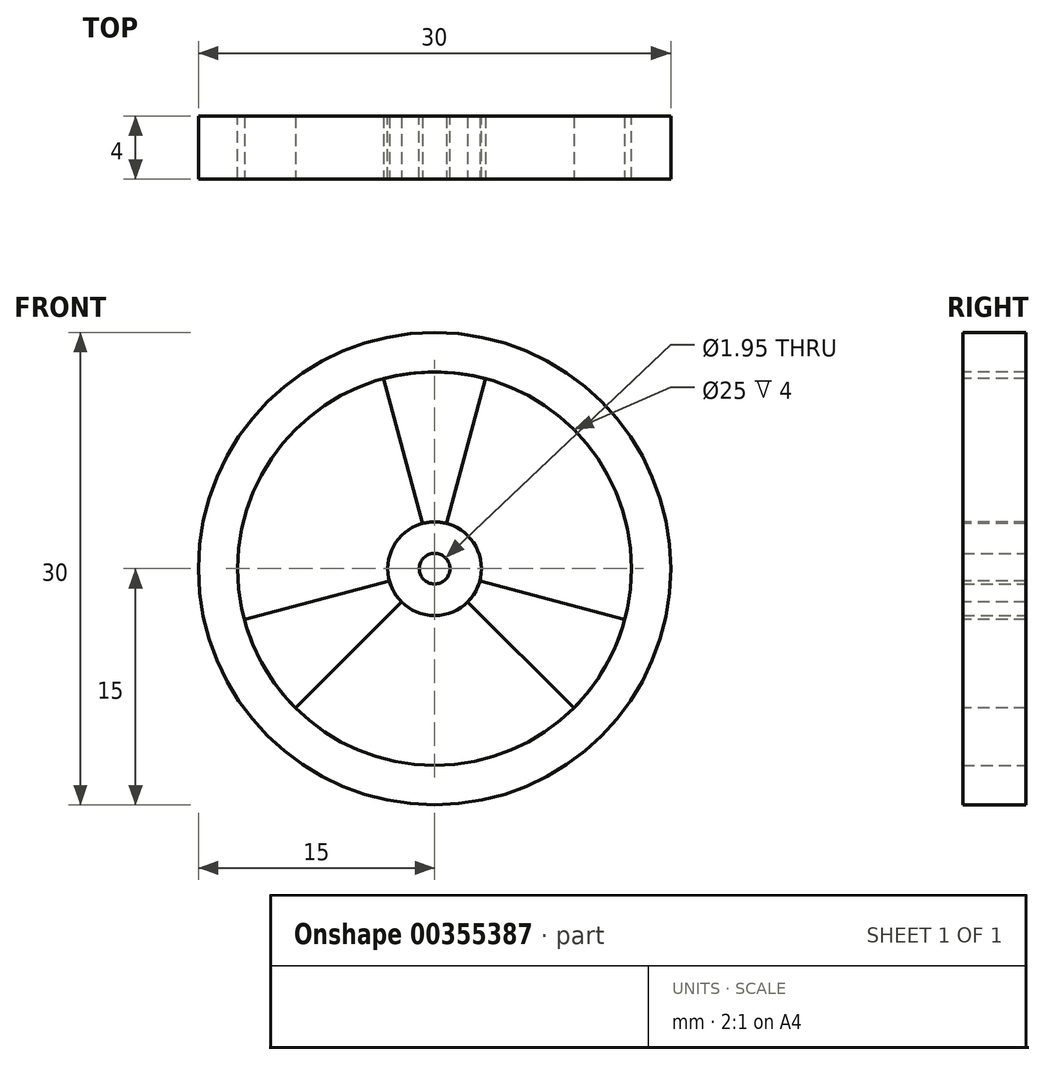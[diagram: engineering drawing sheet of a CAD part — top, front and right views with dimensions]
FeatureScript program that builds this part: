
annotation { "Feature Type Name" : "Feature", "Feature Type Description" : "" }
export const myFeature = defineFeature(function(context is Context, id is Id, definition is map)
    precondition{}
    {
        {
            var Q0;
            Q0=qCreatedBy(makeId("Front.planeOp"),FACE);
            var sketch = newSketch(context, id + "F0", { "sketchPlane" : qUnion([Q0])});
            skCircle(sketch, "E0", {"center": v(0, 0) * mm, "radius": 15 * mm});
            skCircle(sketch, "E1", {"center": v(0, 0) * mm, "radius": 0.97 * mm});
            skCircle(sketch, "E2", {"center": v(0, 0) * mm, "radius": 2.98 * mm});
            skCircle(sketch, "E3", {"center": v(0, 0) * mm, "radius": 12.5 * mm});
            skSolve(sketch);
        }
        {
            var Q0;
            Q0=qSketchRegion(id+"F0",true);
            var Q1;
            Q1=makeQuery(id+"F0.imprint","IMPRINT",FACE,{"disambiguationData":[TD([[makeQuery(id+"F0.imprint","IMPRINT",EDGE,{"derivedFrom":sQuery(id+"F0.wireOp",EDGE,"E1")}),-1.0]])]});
            extrude(context, id + "F1", {"entities" : qUnion([Q0, Q1]), "depth" : 4 * mm});
        }
        {
            var Q0;
            Q0=makeQuery(id+"F1.opExtrude","CAP_FACE",FACE,{"disambiguationData":[OSD([sQuery(id+"F0.wireOp",EDGE,"E0"),sQuery(id+"F0.wireOp",EDGE,"E1")])],"isStart":false});
            var sketch = newSketch(context, id + "F2", { "sketchPlane" : qUnion([Q0])});
            skArc(sketch, "E4", {"start": v(0.77, 2.87) * mm, "mid": v(0, 2.98) * mm, "end": v(-0.77, 2.87) * mm});
            skArc(sketch, "E5", {"start": v(3.24, 12.07) * mm, "mid": v(0, 12.5) * mm, "end": v(-3.24, 12.07) * mm});
            skLineSegment(sketch, "E6", {"start": v(0.77, 2.87) * mm, "end": v(3.24, 12.07) * mm});
            skLineSegment(sketch, "E7", {"start": v(3.24, 12.07) * mm, "end": v(0.77, 2.87) * mm});
            skLineSegment(sketch, "E8", {"start": v(-0.77, 2.87) * mm, "end": v(-3.24, 12.07) * mm});
            skSolve(sketch);
        }
        {
            var Q0;
            Q0=qSketchRegion(id+"F2",true);
            extrude(context, id + "F3", {"entities" : qUnion([Q0]), "oppositeDirection" : true, "depth" : 4 * mm});
        }
        {
            var Q0;
            Q0=makeQuery(id+"F3.opExtrude","SWEPT_BODY",BODY,{"disambiguationData":[OSD([sQuery(id+"F2.wireOp",EDGE,"E4"),sQuery(id+"F2.wireOp",EDGE,"E5"),sQuery(id+"F2.wireOp",EDGE,"E7"),sQuery(id+"F2.wireOp",EDGE,"E8")])]});
            var Q1;
            Q1=makeQuery(id+"F1.opExtrude","CAP_EDGE",EDGE,{"disambiguationData":[OSD([sQuery(id+"F0.wireOp",EDGE,"E2")])],"isStart":true});
            circularPattern(context, id + "F4", {"entities" : qUnion([Q0]), "axis" : qUnion([Q1]), "angle" : 360 * degree, "instanceCount" : 3, "equalSpace" : true});
        }
    });
